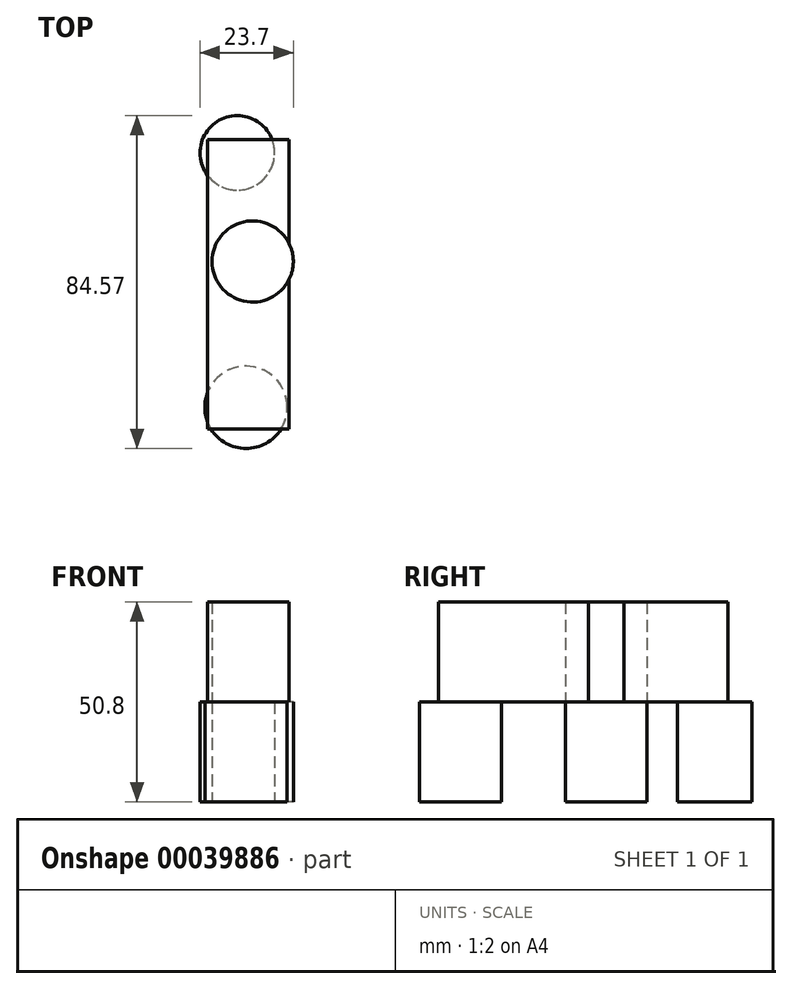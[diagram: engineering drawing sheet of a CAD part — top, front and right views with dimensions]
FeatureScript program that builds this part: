
annotation { "Feature Type Name" : "Feature", "Feature Type Description" : "" }
export const myFeature = defineFeature(function(context is Context, id is Id, definition is map)
    precondition{}
    {
        {
            var Q0;
            Q0=qCreatedBy(makeId("Top.planeOp"),FACE);
            var sketch = newSketch(context, id + "F0", { "sketchPlane" : qUnion([Q0])});
            skCircle(sketch, "E0", {"center": v(-38.05, 0) * mm, "radius": 10.32 * mm});
            skCircle(sketch, "E1", {"center": v(0, 0) * mm, "radius": 7.36 * mm});
            skCircle(sketch, "E2", {"center": v(19.38, -2.23) * mm, "radius": 5.8 * mm});
            skCircle(sketch, "E3", {"center": v(40.84, -3.35) * mm, "radius": 6.97 * mm});
            skSolve(sketch);
        }
        {
            var Q0;
            Q0=makeQuery(id+"F0.imprint","IMPRINT",FACE,{"disambiguationData":[TD([[makeQuery(id+"F0.imprint","IMPRINT",EDGE,{"derivedFrom":sQuery(id+"F0.wireOp",EDGE,"E0")}),1.0]])]});
            extrude(context, id + "F1", {"entities" : qUnion([Q0]), "depth" : 25.4 * mm});
        }
        {
            var Q0;
            Q0=qCreatedBy(makeId("Top.planeOp"),FACE);
            var sketch = newSketch(context, id + "F2", { "sketchPlane" : qUnion([Q0])});
            skCircle(sketch, "E4", {"center": v(-41.96, 27.6) * mm, "radius": 9.47 * mm});
            skSolve(sketch);
        }
        {
            var Q0;
            Q0=makeQuery(id+"F2.imprint","IMPRINT",FACE,{"disambiguationData":[TD([[makeQuery(id+"F2.imprint","IMPRINT",EDGE,{"derivedFrom":sQuery(id+"F2.wireOp",EDGE,"E4")}),1.0]])]});
            extrude(context, id + "F3", {"entities" : qUnion([Q0]), "depth" : 25.4 * mm});
        }
        {
            var Q0;
            Q0=qCreatedBy(makeId("Top.planeOp"),FACE);
            var sketch = newSketch(context, id + "F4", { "sketchPlane" : qUnion([Q0])});
            skCircle(sketch, "E5", {"center": v(-39.75, -37.04) * mm, "radius": 10.46 * mm});
            skSolve(sketch);
        }
        {
            var Q0;
            Q0=makeQuery(id+"F4.imprint","IMPRINT",FACE,{"disambiguationData":[TD([[makeQuery(id+"F4.imprint","IMPRINT",EDGE,{"derivedFrom":sQuery(id+"F4.wireOp",EDGE,"E5")}),1.0]])]});
            extrude(context, id + "F5", {"entities" : qUnion([Q0]), "depth" : 25.4 * mm});
        }
        {
            var Q0;
            Q0=makeQuery(id+"F1.opExtrude","CAP_FACE",FACE,{"disambiguationData":[OSD([sQuery(id+"F0.wireOp",EDGE,"E0")])],"isStart":false});
            var sketch = newSketch(context, id + "F6", { "sketchPlane" : qUnion([Q0])});
            skLineSegment(sketch, "E6.bottom", {"start": v(-49.5, 30.93) * mm, "end": v(-28.77, 30.93) * mm});
            skLineSegment(sketch, "E6.top", {"start": v(-49.5, -42.57) * mm, "end": v(-28.77, -42.57) * mm});
            skLineSegment(sketch, "E6.left", {"start": v(-49.5, 30.93) * mm, "end": v(-49.5, -42.57) * mm});
            skLineSegment(sketch, "E6.right", {"start": v(-28.77, 30.93) * mm, "end": v(-28.77, -42.57) * mm});
            skSolve(sketch);
        }
        {
            var Q0;
            {var subQ5=sQuery(id+"F6.wireOp",EDGE,"E6.bottom");Q0=makeQuery(id+"F6.imprint","IMPRINT",FACE,{"disambiguationData":[TD([[makeQuery(id+"F6.imprint","IMPRINT",EDGE,{"derivedFrom":subQ5}),-1.0]])]});}
            extrude(context, id + "F7", {"entities" : qUnion([Q0]), "depth" : 25.4 * mm});
        }
    });
